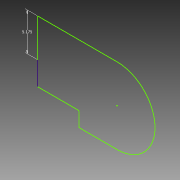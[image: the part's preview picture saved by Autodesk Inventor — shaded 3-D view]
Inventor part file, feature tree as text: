
AUTODESK INVENTOR PART (.ipt)
format: ipt  version: 2014 SP1 (Build 180222100, 222)  size: 79,360 bytes
history: native  units: in
note: dims shown in document units (in); Inventor stores cm internally (conversion verified against a paired STEP export)
features: extrude x1, sketch x1
ambient origin geometry x8: Origin, YZ Plane, XZ Plane, XY Plane, X Axis, Y Axis, Z Axis, Center Point
bodies: Solid1 (feature_tree)
feature tree (2):
  extrude  "Extrusion1"  Depth=0.2228in
  sketch  "Sketch1"  dims[d3=0.2037in d4=0.25in d5=0.2228in d6=0.0in]
